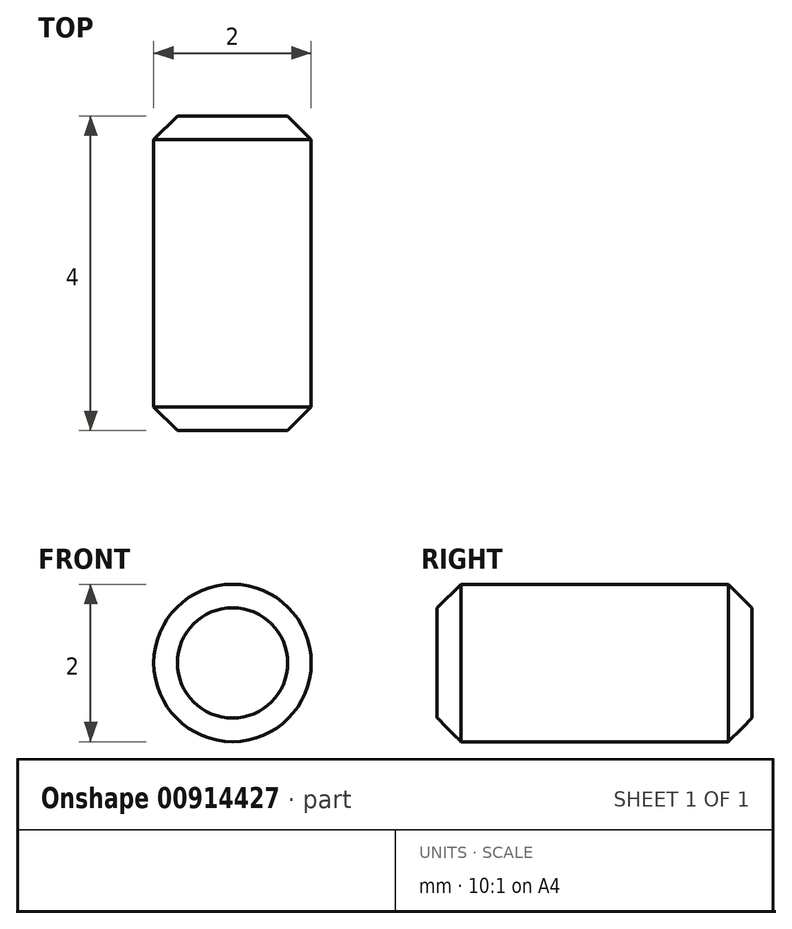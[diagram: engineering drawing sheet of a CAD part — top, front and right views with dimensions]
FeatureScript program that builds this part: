
annotation { "Feature Type Name" : "Feature", "Feature Type Description" : "" }
export const myFeature = defineFeature(function(context is Context, id is Id, definition is map)
    precondition{}
    {
        {
            var Q0;
            Q0=qCreatedBy(makeId("Front.planeOp"),FACE);
            var sketch = newSketch(context, id + "F0", { "sketchPlane" : qUnion([Q0])});
            skCircle(sketch, "E0", {"center": v(0, 0) * mm, "radius": 1 * mm});
            skSolve(sketch);
        }
        {
            var Q0;
            Q0 = qSketchRegion(id + "F0", true);
            extrude(context, id + "F1", {"entities" : qUnion([Q0]), "depth" : 4 * mm, "offsetDistance" : 25 * mm});
        }
        {
            var Q0;
            Q0=makeQuery(id+"F1.opExtrude","CAP_FACE",FACE,{"disambiguationData":[OSD([sQuery(id+"F0.wireOp",EDGE,"E0")])],"isStart":false});
            var Q1;
            Q1=makeQuery(id+"F1.opExtrude","CAP_FACE",FACE,{"disambiguationData":[OSD([sQuery(id+"F0.wireOp",EDGE,"E0")])],"isStart":true});
            chamfer(context, id + "F2", {"entities" : qUnion([Q0, Q1]), "width" : .3 * mm, "tangentPropagation" : true});
        }
    });
